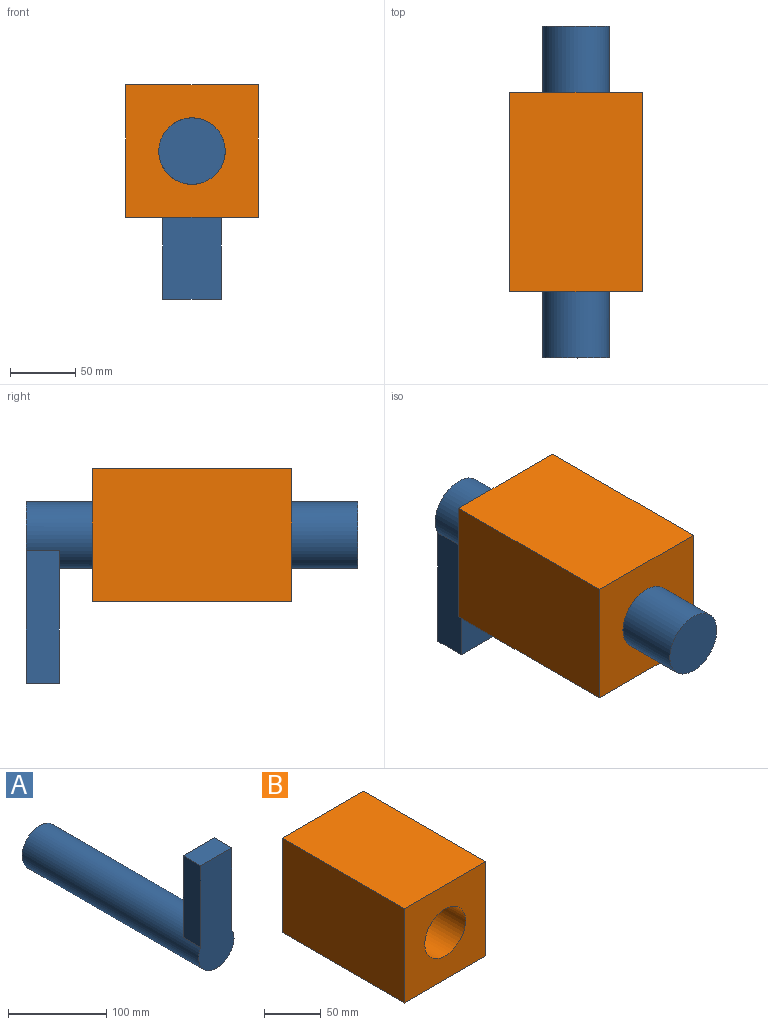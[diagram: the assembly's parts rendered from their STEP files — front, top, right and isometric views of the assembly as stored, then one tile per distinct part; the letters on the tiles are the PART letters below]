
ASSEMBLY  parts=2 mates=1
PART A: 7 faces, bbox 50.8x254x138.8 mm
  f0: cylinder r=25.4mm len=254mm, axis (0,1,0), area 39135.8mm2, adj f1,f2,f3,f4,f5
  f1: plane 138.85x50.8mm, normal (0,-1,0), area 6158.2mm2, adj f0,f3,f5,f6
  f2: plane 50.8x50.8mm, normal (0,1,0), area 2026.8mm2, adj f0
  f3: plane 101.6x25.4mm, normal (1,0,0), area 2580.6mm2, adj f0,f1,f4,f6
  f4: plane 101.6x44.94mm, normal (0,1,0), area 4131.4mm2, adj f0,f3,f5,f6
  f5: plane 101.6x25.4mm, normal (-1,0,0), area 2580.6mm2, adj f0,f1,f4,f6
  f6: plane 44.94x25.4mm, normal (0,0,1), area 1141.4mm2, adj f1,f3,f4,f5
PART B: 7 faces, bbox 101.6x152.4x101.6 mm
  f0: plane 152.4x101.6mm, normal (0,0,1), area 15483.8mm2, adj f1,f4,f5,f6
  f1: plane 152.4x101.6mm, normal (-1,0,0), area 15483.8mm2, adj f0,f2,f5,f6
  f2: plane 152.4x101.6mm, normal (0,0,-1), area 15483.8mm2, adj f1,f4,f5,f6
  f3: cylinder r=25.4mm len=152.4mm, axis (0,1,0), area 24322mm2, adj f5,f6
  f4: plane 152.4x101.6mm, normal (1,0,0), area 15483.8mm2, adj f0,f2,f5,f6
  f5: plane 101.6x101.6mm, normal (0,-1,0), area 8295.7mm2, adj f0,f1,f2,f3,f4
  f6: plane 101.6x101.6mm, normal (0,1,0), area 8295.7mm2, adj f0,f1,f2,f3,f4
PLACE A rot(axis=(1,0,0),180deg) t=(0,0,-50.8)mm
PLACE B t=(0,0,-50.8)mm
MATE revolute A.f0 <-> B.f3  axis (0,-1,0) through (0,0,-50.8)mm
